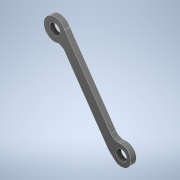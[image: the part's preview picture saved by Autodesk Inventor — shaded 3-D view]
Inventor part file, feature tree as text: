
AUTODESK INVENTOR PART (.ipt)
format: ipt  version: 2022 (Build 260153000, 153)  size: 305,152 bytes
history: native  units: in
note: dims shown in document units (in); Inventor stores cm internally (conversion verified against a paired STEP export)
features: other x1, extrude x1, sketch x1
ambient origin geometry x8: Origin, YZ Plane, XZ Plane, XY Plane, X Axis, Y Axis, Z Axis, Center Point
bodies: Body1 (feature_tree)
feature tree (3):
  other  "Sólido1"
  extrude  "Extrusión1"  Depth=0.0787in
  sketch  "Boceto1"  dims[d7=0.0984in d8=0.1969in d9=0.0984in d11=0.6024in d12=0.687in d15=0.0472in d16=0.0in d18=0.1772in d19=0.0787in d20=0.0945in d21=0.0787in]
